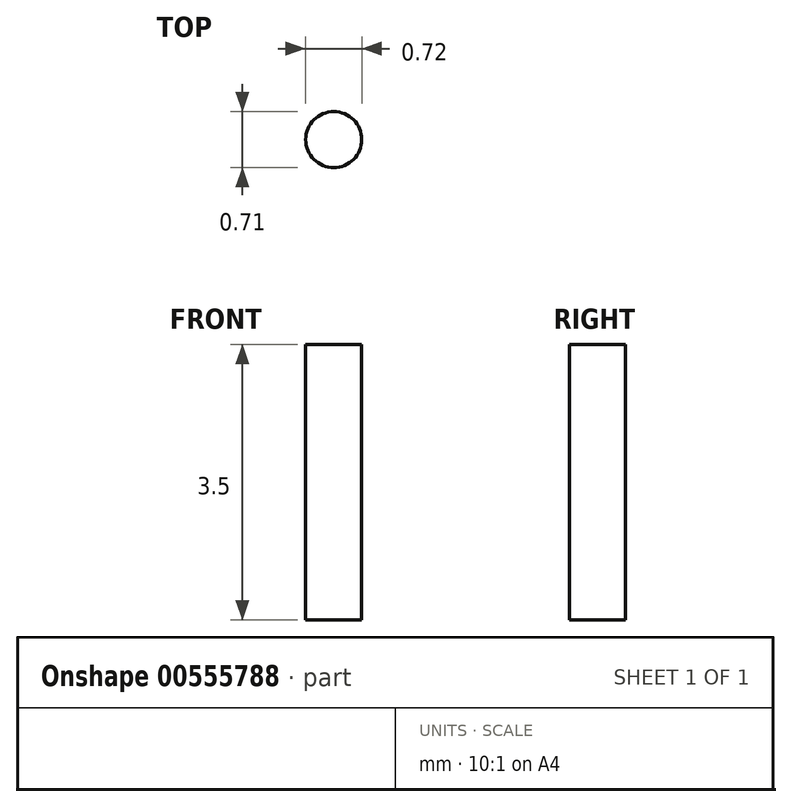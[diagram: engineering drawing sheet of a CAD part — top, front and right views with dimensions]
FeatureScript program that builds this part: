
annotation { "Feature Type Name" : "Feature", "Feature Type Description" : "" }
export const myFeature = defineFeature(function(context is Context, id is Id, definition is map)
    precondition{}
    {
        {
            var Q0;
            Q0=qCreatedBy(makeId("Top.planeOp"),FACE);
            var sketch = newSketch(context, id + "F0", { "sketchPlane" : qUnion([Q0])});
            skLineSegment(sketch, "E0.bottom", {"start": v(-10.02, 12.87) * mm, "end": v(9.98, 12.87) * mm});
            skLineSegment(sketch, "E0.top", {"start": v(-10.02, -13.13) * mm, "end": v(9.98, -13.13) * mm});
            skLineSegment(sketch, "E0.left", {"start": v(-10.02, 12.87) * mm, "end": v(-10.02, -13.13) * mm});
            skLineSegment(sketch, "E0.right", {"start": v(9.98, 12.87) * mm, "end": v(9.98, -13.13) * mm});
            skCircle(sketch, "E1", {"center": v(0, -3.1) * mm, "radius": 8.49 * mm});
            skSolve(sketch);
        }
        {
            var Q0;
            Q0=makeQuery(id+"F0.imprint","IMPRINT",FACE,{"disambiguationData":[TD([[makeQuery(id+"F0.imprint","IMPRINT",EDGE,{"derivedFrom":sQuery(id+"F0.wireOp",EDGE,"E0.bottom")}),-1.0]])]});
            extrude(context, id + "F1", {"entities" : qUnion([Q0]), "depth" : 3.5 * mm, "offsetDistance" : 25 * mm});
        }
        {
            var Q0;
            Q0=makeQuery(id+"F1.opExtrude","SWEPT_FACE",FACE,{"disambiguationData":[OSD([sQuery(id+"F0.wireOp",EDGE,"E0.bottom")])]});
            var sketch = newSketch(context, id + "F2", { "sketchPlane" : qUnion([Q0])});
            skLineSegment(sketch, "E2.bottom", {"start": v(-9.18, 2.9) * mm, "end": v(9.22, 2.9) * mm});
            skLineSegment(sketch, "E2.top", {"start": v(-9.18, 0.6) * mm, "end": v(9.22, 0.6) * mm});
            skLineSegment(sketch, "E2.left", {"start": v(-9.18, 2.9) * mm, "end": v(-9.18, 0.6) * mm});
            skLineSegment(sketch, "E2.right", {"start": v(9.22, 2.9) * mm, "end": v(9.22, 0.6) * mm});
            skSolve(sketch);
        }
        {
            var Q0;
            Q0=makeQuery(id+"F2.imprint","IMPRINT",FACE,{"disambiguationData":[TD([[makeQuery(id+"F2.imprint","IMPRINT",EDGE,{"derivedFrom":sQuery(id+"F2.wireOp",EDGE,"E2.bottom")}),-1.0]])]});
            extrude(context, id + "F3", {"entities" : qUnion([Q0]), "operationType" : NewBodyOperationType.REMOVE, "oppositeDirection" : true, "depth" : 1.6 * mm, "offsetDistance" : 25 * mm});
        }
        {
            var Q0;
            Q0=makeQuery(id+"F1.opExtrude","CAP_FACE",FACE,{"disambiguationData":[OSD([sQuery(id+"F0.wireOp",EDGE,"E0.bottom"),sQuery(id+"F0.wireOp",EDGE,"E0.top"),sQuery(id+"F0.wireOp",EDGE,"E0.left"),sQuery(id+"F0.wireOp",EDGE,"E0.right"),sQuery(id+"F0.wireOp",EDGE,"E1")])],"isStart":false});
            var sketch = newSketch(context, id + "F4", { "sketchPlane" : qUnion([Q0])});
            skFitSpline(sketch, "E3", {"points": [v(-9.07, 10.31) * mm, v(-8.45, 8.33) * mm, v(-8.34, 8.3) * mm, v(-7.1, 9.77) * mm, v(-7.11, 9.83) * mm, v(-8.62, 10.48) * mm, v(-9.07, 10.31) * mm]});
            skLineSegment(sketch, "E4", {"start": v(-6.39, 11.23) * mm, "end": v(-6.39, 5.39) * mm});
            skFitSpline(sketch, "E5.MirrorC", {"points": [v(-3.71, 10.31) * mm, v(-4.33, 8.33) * mm, v(-4.44, 8.3) * mm, v(-5.67, 9.77) * mm, v(-5.67, 9.83) * mm, v(-4.16, 10.48) * mm, v(-3.71, 10.31) * mm]});
            skFitSpline(sketch, "E6", {"points": [v(-8.22, 7.86) * mm, v(-8.16, 7.98) * mm, v(-7.03, 7.81) * mm, v(-6.75, 7) * mm, v(-6.63, 5.32) * mm, v(-6.63, 5.32) * mm, v(-8.22, 7.86) * mm]});
            skFitSpline(sketch, "E7.MirrorC", {"points": [v(-4.56, 7.86) * mm, v(-4.62, 7.98) * mm, v(-5.75, 7.81) * mm, v(-6.03, 7) * mm, v(-6.15, 5.32) * mm, v(-6.15, 5.32) * mm, v(-4.56, 7.86) * mm]});
            skCircle(sketch, "E8", {"center": v(-6.96, 8.36) * mm, "radius": 0.36 * mm});
            skCircle(sketch, "E9.MirrorC", {"center": v(-5.82, 8.36) * mm, "radius": 0.36 * mm});
            skSolve(sketch);
        }
        {
            var Q0;
            Q0=makeQuery(id+"F4.imprint","IMPRINT",FACE,{"disambiguationData":[TD([[makeQuery(id+"F4.imprint","IMPRINT",EDGE,{"derivedFrom":sQuery(id+"F4.wireOp",EDGE,"E3")}),1.0]])]});
            var Q1;
            Q1=makeQuery(id+"F4.imprint","IMPRINT",FACE,{"disambiguationData":[TD([[makeQuery(id+"F4.imprint","IMPRINT",EDGE,{"derivedFrom":sQuery(id+"F4.wireOp",EDGE,"E5.MirrorC")}),-1.0]])]});
            var Q2;
            Q2=makeQuery(id+"F4.imprint","IMPRINT",FACE,{"disambiguationData":[TD([[makeQuery(id+"F4.imprint","IMPRINT",EDGE,{"derivedFrom":sQuery(id+"F4.wireOp",EDGE,"E6")}),-1.0]])]});
            var Q3;
            Q3=makeQuery(id+"F4.imprint","IMPRINT",FACE,{"disambiguationData":[TD([[makeQuery(id+"F4.imprint","IMPRINT",EDGE,{"derivedFrom":sQuery(id+"F4.wireOp",EDGE,"E7.MirrorC")}),1.0]])]});
            extrude(context, id + "F5", {"entities" : qUnion([Q0, Q1, Q2, Q3]), "operationType" : NewBodyOperationType.REMOVE, "oppositeDirection" : true, "depth" : 25 * mm, "offsetDistance" : 25 * mm});
        }
        {
            var Q0;
            Q0=makeQuery(id+"F4.imprint","IMPRINT",FACE,{"disambiguationData":[TD([[makeQuery(id+"F4.imprint","IMPRINT",EDGE,{"derivedFrom":sQuery(id+"F4.wireOp",EDGE,"E8")}),1.0]])]});
            var Q1;
            Q1=makeQuery(id+"F4.imprint","IMPRINT",FACE,{"disambiguationData":[TD([[makeQuery(id+"F4.imprint","IMPRINT",EDGE,{"derivedFrom":sQuery(id+"F4.wireOp",EDGE,"E9.MirrorC")}),-1.0]])]});
            extrude(context, id + "F6", {"entities" : qUnion([Q0, Q1]), "operationType" : NewBodyOperationType.REMOVE, "oppositeDirection" : true, "depth" : 25 * mm, "offsetDistance" : 25 * mm});
        }
    });
